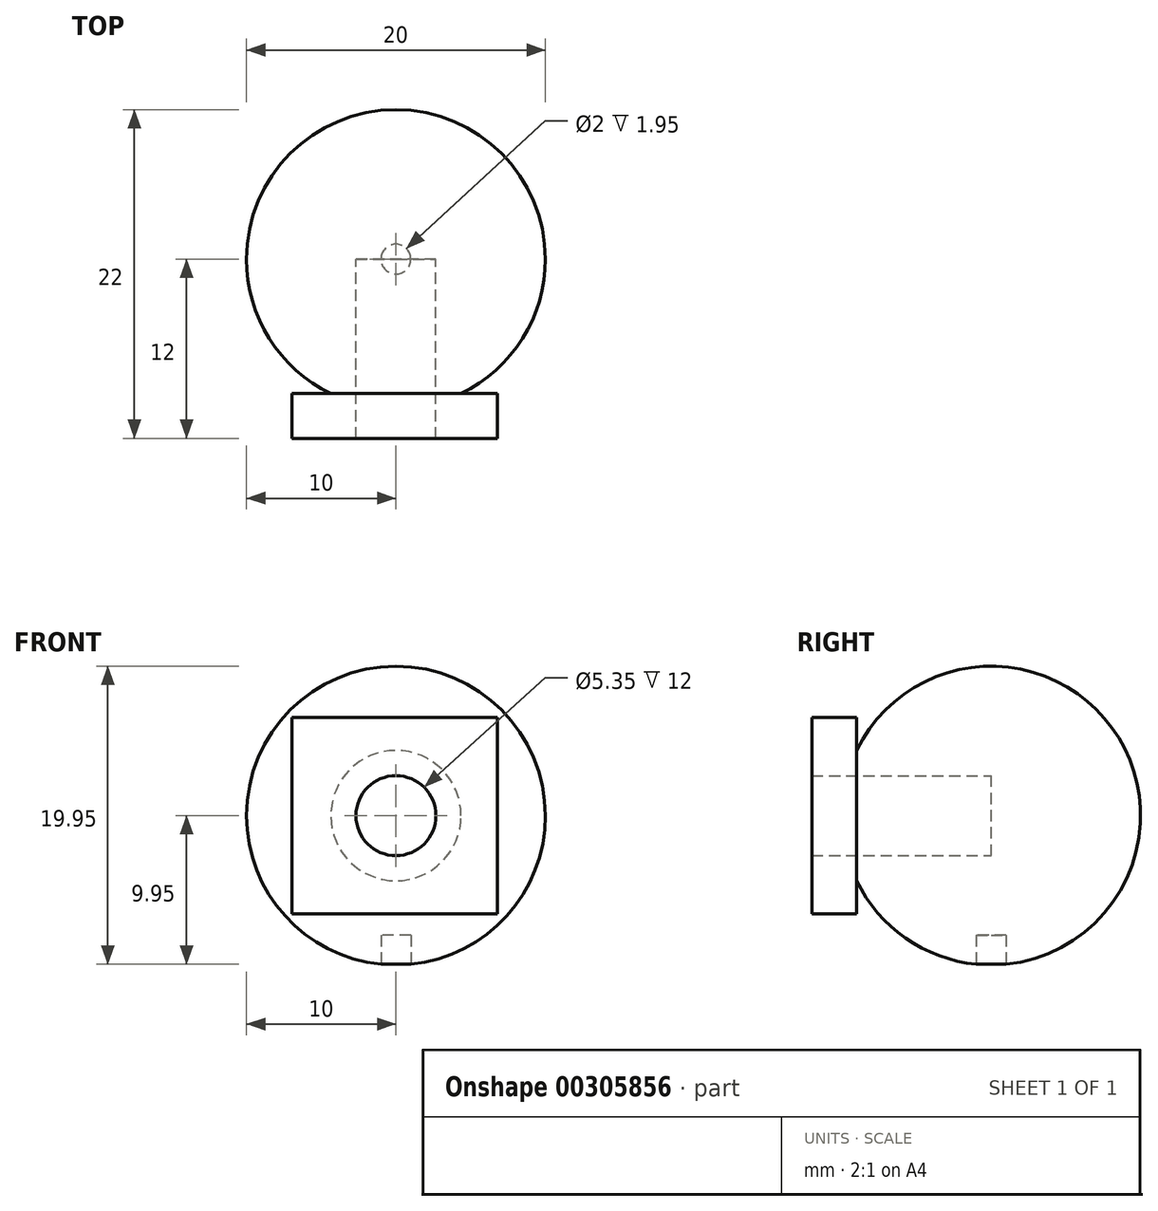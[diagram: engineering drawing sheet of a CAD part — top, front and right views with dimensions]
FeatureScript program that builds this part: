
annotation { "Feature Type Name" : "Feature", "Feature Type Description" : "" }
export const myFeature = defineFeature(function(context is Context, id is Id, definition is map)
    precondition{}
    {
        {
            var Q0;
            Q0=qCreatedBy(makeId("Front.planeOp"),FACE);
            var sketch = newSketch(context, id + "F0", { "sketchPlane" : qUnion([Q0])});
            skPoint(sketch, "E0.endSnap0", {"position": v(0, -12.5) * mm});
            skArc(sketch, "E1", {"start": v(-10, 0) * mm, "mid": v(0, -10) * mm, "end": v(10, 0) * mm});
            skLineSegment(sketch, "E2", {"start": v(-10, 0) * mm, "end": v(10, 0) * mm});
            skSolve(sketch);
        }
        {
            var Q0;
            Q0=makeQuery(id+"F0.imprint","IMPRINT",FACE,{"disambiguationData":[TD([[makeQuery(id+"F0.imprint","IMPRINT",EDGE,{"derivedFrom":sQuery(id+"F0.wireOp",EDGE,"E1")}),1.0]])]});
            var Q1;
            Q1=sQuery(id+"F0.wireOp",EDGE,"E2");
            revolve(context, id + "F1", {"entities" : qUnion([Q0]), "axis" : qUnion([Q1]), "revolveType" : RevolveType.FULL});
        }
        {
            var Q0;
            Q0=qCreatedBy(makeId("Front.planeOp"),FACE);
            var sketch = newSketch(context, id + "F2", { "sketchPlane" : qUnion([Q0])});
            skCircle(sketch, "E3", {"center": v(0, 0) * mm, "radius": 2.67 * mm});
            skSolve(sketch);
        }
        {
            var Q0;
            Q0=qCreatedBy(makeId("Right.planeOp"),FACE);
            cPlane(context, id + "F3", {"entities" : qUnion([Q0]), "cplaneType" : CPlaneType.OFFSET, "offset" : 10 * mm, "width" : 150 * mm, "height" : 150 * mm});
        }
        {
            var Q0;
            Q0=qCreatedBy(makeId("Top.planeOp"),FACE);
            cPlane(context, id + "F4", {"entities" : qUnion([Q0]), "cplaneType" : CPlaneType.OFFSET, "offset" : 10 * mm, "oppositeDirection" : true, "width" : 150 * mm, "height" : 150 * mm});
        }
        {
            var Q0;
            Q0=qCreatedBy(makeId("Right.planeOp"),FACE);
            cPlane(context, id + "F5", {"entities" : qUnion([Q0]), "cplaneType" : CPlaneType.OFFSET, "offset" : 10 * mm, "oppositeDirection" : true, "width" : 150 * mm, "height" : 150 * mm});
        }
        {
            var Q0;
            Q0=qCreatedBy(id+"F4.planeOp",FACE);
            var sketch = newSketch(context, id + "F6", { "sketchPlane" : qUnion([Q0])});
            skCircle(sketch, "E4", {"center": v(0, 0) * mm, "radius": 1 * mm});
            skSolve(sketch);
        }
        {
            var Q0;
            Q0=qSketchRegion(id+"F6",true);
            extrude(context, id + "F7", {"entities" : qUnion([Q0]), "operationType" : NewBodyOperationType.REMOVE, "depth" : 2 * mm});
        }
        {
            var Q0;
            Q0=qCreatedBy(makeId("Front.planeOp"),FACE);
            cPlane(context, id + "F8", {"entities" : qUnion([Q0]), "cplaneType" : CPlaneType.OFFSET, "offset" : 9 * mm, "width" : 150 * mm, "height" : 150 * mm});
        }
        {
            var Q0;
            Q0=qCreatedBy(id+"F8.planeOp",FACE);
            var sketch = newSketch(context, id + "F9", { "sketchPlane" : qUnion([Q0])});
            skLineSegment(sketch, "E5.bottom", {"start": v(6.78, 6.58) * mm, "end": v(-6.96, 6.58) * mm});
            skLineSegment(sketch, "E5.top", {"start": v(6.78, -6.58) * mm, "end": v(-6.96, -6.58) * mm});
            skLineSegment(sketch, "E5.left", {"start": v(6.78, 6.58) * mm, "end": v(6.78, -6.58) * mm});
            skLineSegment(sketch, "E5.right", {"start": v(-6.96, 6.58) * mm, "end": v(-6.96, -6.58) * mm});
            skSolve(sketch);
        }
        {
            var Q0;
            Q0=qSketchRegion(id+"F9",true);
            extrude(context, id + "F10", {"entities" : qUnion([Q0]), "operationType" : NewBodyOperationType.ADD, "depth" : 3 * mm});
        }
        {
            var Q0;
            Q0=qSketchRegion(id+"F2",true);
            var Q1;
            Q1=sQuery(id+"F2.wireOp",EDGE,"E3");
            extrude(context, id + "F11", {"entities" : qUnion([Q0]), "operationType" : NewBodyOperationType.REMOVE, "surfaceEntities" : qUnion([Q1]), "endBound" : BoundingType.THROUGH_ALL, "depth" : 50 * mm});
        }
        {
            var Q0;
            Q0=qCreatedBy(makeId("Top.planeOp"),FACE);
            cPlane(context, id + "F12", {"entities" : qUnion([Q0]), "cplaneType" : CPlaneType.OFFSET, "offset" : 10 * mm, "width" : 150 * mm, "height" : 150 * mm});
        }
    });
